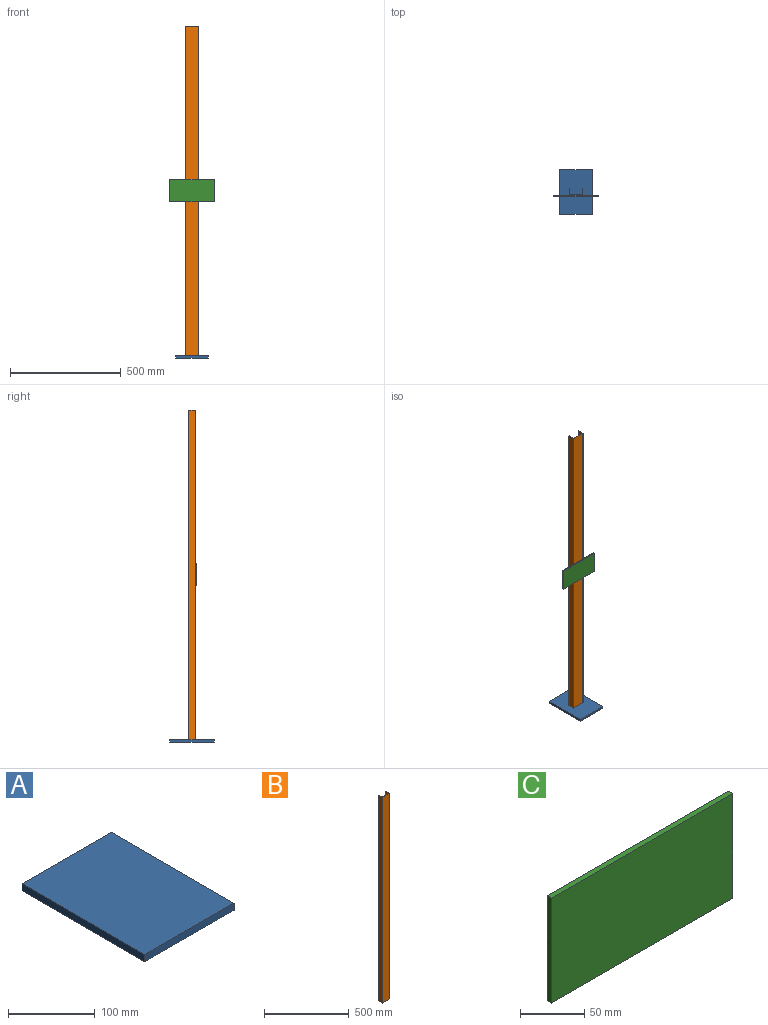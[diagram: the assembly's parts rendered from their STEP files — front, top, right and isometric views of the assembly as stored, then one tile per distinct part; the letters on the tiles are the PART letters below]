
ASSEMBLY  parts=3 mates=2
PART A: 6 faces, bbox 145x200x10 mm
  f0: plane 200x10mm, normal (1,0,0), area 2000mm2, adj f1,f3,f4,f5
  f1: plane 145x10mm, normal (0,1,0), area 1450mm2, adj f0,f2,f4,f5
  f2: plane 200x10mm, normal (-1,0,0), area 2000mm2, adj f1,f3,f4,f5
  f3: plane 145x10mm, normal (0,-1,0), area 1450mm2, adj f0,f2,f4,f5
  f4: plane 200x145mm, normal (0,0,1), area 29000mm2, adj f0,f1,f2,f3
  f5: plane 200x145mm, normal (0,0,-1), area 29000mm2, adj f0,f1,f2,f3
PART B: 10 faces, bbox 60x30x1490 mm
  f0: plane 1490x56mm, normal (0,1,0), area 83440mm2, adj f1,f7,f8,f9
  f1: plane 1490x28mm, normal (1,0,0), area 41720mm2, adj f0,f2,f8,f9
  f2: plane 1490x2mm, normal (0,1,0), area 2980mm2, adj f1,f3,f8,f9
  f3: plane 1490x30mm, normal (-1,0,0), area 44700mm2, adj f2,f4,f8,f9
  f4: plane 1490x60mm, normal (0,-1,0), area 89400mm2, adj f3,f5,f8,f9
  f5: plane 1490x30mm, normal (1,0,0), area 44700mm2, adj f4,f6,f8,f9
  f6: plane 1490x2mm, normal (0,1,0), area 2980mm2, adj f5,f7,f8,f9
  f7: plane 1490x28mm, normal (-1,0,0), area 41720mm2, adj f0,f6,f8,f9
  f8: plane 60x30mm, normal (0,0,1), area 232mm2, adj f0,f1,f2,f3,f4,f5,f6,f7
  f9: plane 60x30mm, normal (0,0,-1), area 232mm2, adj f0,f1,f2,f3,f4,f5,f6,f7
PART C: 6 faces, bbox 200x5x100 mm
  f0: plane 100x5mm, normal (1,0,0), area 500mm2, adj f1,f3,f4,f5
  f1: plane 200x5mm, normal (0,0,1), area 1000mm2, adj f0,f2,f4,f5
  f2: plane 100x5mm, normal (-1,0,0), area 500mm2, adj f1,f3,f4,f5
  f3: plane 200x5mm, normal (0,0,-1), area 1000mm2, adj f0,f2,f4,f5
  f4: plane 200x100mm, normal (0,-1,0), area 20000mm2, adj f0,f1,f2,f3
  f5: plane 200x100mm, normal (0,1,0), area 20000mm2, adj f0,f1,f2,f3
PLACE A t=(-167.52,-218.54,-634.85)mm
PLACE B t=(-197.52,-233.54,-624.85)mm
PLACE C t=(-167.52,-233.54,120.15)mm
MATE fastened C.f5 <-> B.f4  axis (0,1,0) through (-167.52,-233.54,120.15)mm
MATE fastened B.f9 <-> A.f4  axis (0,0,-1) through (-137.52,-218.54,-624.85)mm
